# Revit family: FlushPlateControlPanel-12cm-SmartPanel-Vitra-VCareSeries-742-15
name_source: partatom
category: Plumbing Fixtures
revit_build: Autodesk Revit 2017 (Build: 20160225_1515(x64)
units: mm (PartAtom-declared; Revit-internal decimal feet)

## family parameters
Cut with Voids When Loaded = No
Host = Face
OmniClass Number = 23.45.00.00
OmniClass Title = Sanitary, Laundry, and Cleaning Equipment
Part Type = Normal
Room Calculation Point = No
Round Connector Dimension = Use Diameter
Shared = Yes

## types (1)
- FlushPlateControlPanel-SmartPanel-Vitra-VCareSeries_742-1501
    Article No. (default) = 742-1501
    BIMobject category = Toilet Cisterns
    Brand = VitrA
    CW Connection = No
    Coating Material = Matte Black
    Color = Black
    Default Elevation = 0 mm  [stored 0 ft]
    Description = VitrA WC Cisterns Control Panel - Smart Panel
Compatible with Regular Frames (742-frames)
    Design country = Turkey
    HW Connection = No
    IFC Classification = Sanitary Terminal
    Installation instructions = https://www.vitraglobal.com
    Main Material = Metal
    Manufacturer = Vitra
    Manufacturer name = Vitra
    Masterformat 2014 Code = 22 00 00
    Masterformat 2014 Description = Plumbing
    Model = 742-1501
    Mounting type = Wall Mounted
    NBS Referans Code = 31-75
    NBS Referans Description = Sanitary Accessories
    Nominal Depth (mm) = 12 mm  [stored 0.0393701 ft]
    Nominal Height (mm) = 159 mm
    Nominal Width (mm) = 238 mm
    OmniClass Code = 23-31 00 00
    OmniClass Description = Plumbing Specific Products and Equipment
    Product Properties = Vitra V-Care Control Panel
    Product SKU = 742-1501
    Product certification = https://www.vitraglobal.com
    Product family = V-Care
    Product group = WC Cisterns Control Panel
    Product url = https://www.vitraglobal.com
    Technical description = https://www.vitraglobal.com
    UNSPSC Description = Plumbing connectors
    URL = https://www.vitra.com.tr
    Uniclass 1.4 Code = L71111
    Uniclass 1.4 Description = Packaged plumbing units
    Uniclass 2.0 Code = PR-31-75
    Uniclass 2.0 Description = Sanitary Accessories
    Uniclass 2015 Code = Pr_40_20_76
    Uniclass 2015 Name = Sanitary accessories
    Uniformat II Code = D20
    Uniformat II Description = PLUMBING
    Vent Connection = No
    Warranty Period (Year) = 2 Years
    Waste Connection = No
    Weight Net (kg) = 1.54
    Youtube = https://www.youtube.com

note: [stored X ft] marks values corroborated as IEEE doubles in the binary element streams (Revit-internal decimal feet)

## geometry (parser evidence)
native form markers: Sweep x1
no freeform markers — native parametric forms only
